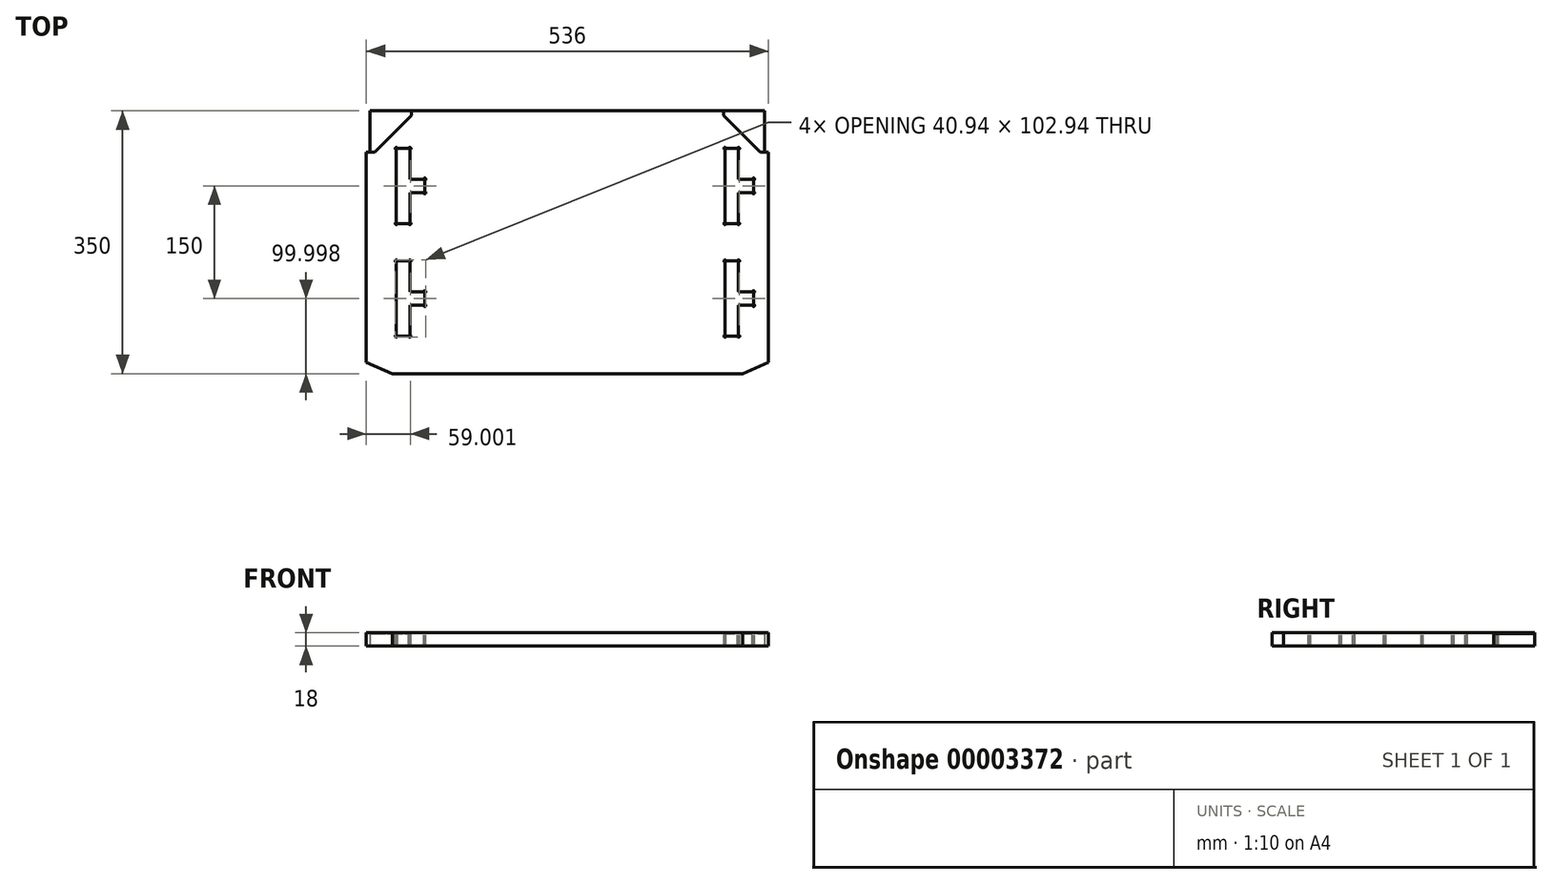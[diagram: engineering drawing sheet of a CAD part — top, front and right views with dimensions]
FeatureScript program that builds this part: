
annotation { "Feature Type Name" : "Feature", "Feature Type Description" : "" }
export const myFeature = defineFeature(function(context is Context, id is Id, definition is map)
    precondition{}
    {
        {
            var Q0;
            Q0=qCreatedBy(makeId("Top.planeOp"),FACE);
            var sketch = newSketch(context, id + "F0", { "sketchPlane" : qUnion([Q0])});
            skLineSegment(sketch, "E0.bottom", {"start": v(-215.74, -76.17) * mm, "end": v(320.26, -76.17) * mm});
            skLineSegment(sketch, "E0.top", {"start": v(-210.74, 273.83) * mm, "end": v(315.26, 273.83) * mm});
            skLineSegment(sketch, "E0.left", {"start": v(-215.74, -76.17) * mm, "end": v(-215.74, 218.83) * mm});
            skLineSegment(sketch, "E0.right", {"start": v(320.26, -76.17) * mm, "end": v(320.26, 218.83) * mm});
            skLineSegment(sketch, "E1.bottom", {"start": v(-175.74, -26.17) * mm, "end": v(-157.74, -26.17) * mm});
            skLineSegment(sketch, "E1.top", {"start": v(-175.74, 73.83) * mm, "end": v(-157.74, 73.83) * mm});
            skLineSegment(sketch, "E1.left", {"start": v(-175.74, -26.17) * mm, "end": v(-175.74, 73.83) * mm});
            skLineSegment(sketch, "E1.right", {"start": v(-157.74, -26.17) * mm, "end": v(-157.74, 14.83) * mm});
            skLineSegment(sketch, "E2.bottom", {"start": v(-175.74, 123.83) * mm, "end": v(-157.74, 123.83) * mm});
            skLineSegment(sketch, "E2.top", {"start": v(-175.74, 223.83) * mm, "end": v(-157.74, 223.83) * mm});
            skLineSegment(sketch, "E2.left", {"start": v(-175.74, 123.83) * mm, "end": v(-175.74, 223.83) * mm});
            skLineSegment(sketch, "E2.right", {"start": v(-157.74, 123.83) * mm, "end": v(-157.74, 164.83) * mm});
            skLineSegment(sketch, "E3.bottom", {"start": v(280.26, -26.17) * mm, "end": v(262.26, -26.17) * mm});
            skLineSegment(sketch, "E3.top", {"start": v(280.26, 73.83) * mm, "end": v(262.26, 73.83) * mm});
            skLineSegment(sketch, "E3.left", {"start": v(280.26, -26.17) * mm, "end": v(280.26, 14.83) * mm});
            skLineSegment(sketch, "E4.bottom", {"start": v(262.26, 223.83) * mm, "end": v(280.26, 223.83) * mm});
            skLineSegment(sketch, "E4.top", {"start": v(262.26, 123.83) * mm, "end": v(280.26, 123.83) * mm});
            skLineSegment(sketch, "E4.right", {"start": v(280.26, 223.83) * mm, "end": v(280.26, 182.83) * mm});
            skLineSegment(sketch, "E5", {"start": v(-157.74, 14.83) * mm, "end": v(-137.74, 14.83) * mm});
            skLineSegment(sketch, "E6", {"start": v(-137.74, 14.83) * mm, "end": v(-137.74, 32.83) * mm});
            skLineSegment(sketch, "E7", {"start": v(-137.74, 32.83) * mm, "end": v(-157.74, 32.83) * mm});
            skLineSegment(sketch, "E8.trimOffspring", {"start": v(-157.74, 32.83) * mm, "end": v(-157.74, 73.83) * mm});
            skLineSegment(sketch, "E9", {"start": v(-157.74, 164.83) * mm, "end": v(-137.74, 164.83) * mm});
            skLineSegment(sketch, "E10", {"start": v(-137.74, 164.83) * mm, "end": v(-137.74, 182.83) * mm});
            skLineSegment(sketch, "E11", {"start": v(-137.74, 182.83) * mm, "end": v(-157.74, 182.83) * mm});
            skLineSegment(sketch, "E12.trimOffspring", {"start": v(-157.74, 182.83) * mm, "end": v(-157.74, 223.83) * mm});
            skLineSegment(sketch, "E13", {"start": v(262.26, -26.17) * mm, "end": v(262.26, 73.83) * mm});
            skLineSegment(sketch, "E14", {"start": v(262.26, 123.83) * mm, "end": v(262.26, 223.83) * mm});
            skLineSegment(sketch, "E15.bottom", {"start": v(280.26, 14.83) * mm, "end": v(300.26, 14.83) * mm});
            skLineSegment(sketch, "E15.top", {"start": v(280.26, 32.83) * mm, "end": v(300.26, 32.83) * mm});
            skLineSegment(sketch, "E15.right", {"start": v(300.26, 14.83) * mm, "end": v(300.26, 32.83) * mm});
            skLineSegment(sketch, "E16.bottom", {"start": v(280.26, 164.83) * mm, "end": v(300.26, 164.83) * mm});
            skLineSegment(sketch, "E16.top", {"start": v(280.26, 182.83) * mm, "end": v(300.26, 182.83) * mm});
            skLineSegment(sketch, "E16.right", {"start": v(300.26, 164.83) * mm, "end": v(300.26, 182.83) * mm});
            skLineSegment(sketch, "E17.trimOffspring", {"start": v(280.26, 32.83) * mm, "end": v(280.26, 73.83) * mm});
            skLineSegment(sketch, "E18.trimOffspring", {"start": v(280.26, 164.83) * mm, "end": v(280.26, 123.83) * mm});
            skLineSegment(sketch, "E19.top", {"start": v(320.26, 218.83) * mm, "end": v(315.26, 218.83) * mm});
            skLineSegment(sketch, "E19.right", {"start": v(315.26, 273.83) * mm, "end": v(315.26, 218.83) * mm});
            skPoint(sketch, "E19.bottom.start.orphan", {"position": v(320.26, 273.83) * mm});
            skLineSegment(sketch, "E20.top", {"start": v(-215.74, 218.83) * mm, "end": v(-210.74, 218.83) * mm});
            skLineSegment(sketch, "E20.right", {"start": v(-210.74, 273.83) * mm, "end": v(-210.74, 218.83) * mm});
            skSolve(sketch);
        }
        {
            var Q0;
            Q0=makeQuery(id+"F0.imprint","IMPRINT",FACE,{"disambiguationData":[TD([[makeQuery(id+"F0.imprint","IMPRINT",EDGE,{"derivedFrom":sQuery(id+"F0.wireOp",EDGE,"E0.bottom")}),1.0]])]});
            extrude(context, id + "F1", {"entities" : qUnion([Q0]), "depth" : 18 * mm});
        }
        {
            var Q0;
            Q0=makeQuery(id+"F1.opExtrude","SWEPT_EDGE",EDGE,{"disambiguationData":[OSD([sQuery(id+"F0.wireOp",EDGE,"E0.bottom"),sQuery(id+"F0.wireOp",EDGE,"E0.left")])]});
            var Q1;
            Q1=makeQuery(id+"F1.opExtrude","SWEPT_EDGE",EDGE,{"disambiguationData":[OSD([sQuery(id+"F0.wireOp",EDGE,"E0.bottom"),sQuery(id+"F0.wireOp",EDGE,"E0.right")])]});
            chamfer(context, id + "F2", {"entities" : qUnion([Q0, Q1]), "chamferType" : ChamferType.TWO_OFFSETS, "width1" : 15 * mm, "oppositeDirection" : true, "width2" : 34.5 * mm, "tangentPropagation" : true});
        }
        {
            var Q0;
            Q0=makeQuery(id+"F1.opExtrude","CAP_FACE",FACE,{"disambiguationData":[OSD([sQuery(id+"F0.wireOp",EDGE,"E0.bottom"),sQuery(id+"F0.wireOp",EDGE,"E0.top"),sQuery(id+"F0.wireOp",EDGE,"E0.left"),sQuery(id+"F0.wireOp",EDGE,"E0.right"),sQuery(id+"F0.wireOp",EDGE,"E1.bottom"),sQuery(id+"F0.wireOp",EDGE,"E1.top"),sQuery(id+"F0.wireOp",EDGE,"E1.left"),sQuery(id+"F0.wireOp",EDGE,"E1.right"),sQuery(id+"F0.wireOp",EDGE,"E2.bottom"),sQuery(id+"F0.wireOp",EDGE,"E2.top"),sQuery(id+"F0.wireOp",EDGE,"E2.left"),sQuery(id+"F0.wireOp",EDGE,"E2.right"),sQuery(id+"F0.wireOp",EDGE,"E3.bottom"),sQuery(id+"F0.wireOp",EDGE,"E3.top"),sQuery(id+"F0.wireOp",EDGE,"E3.left"),sQuery(id+"F0.wireOp",EDGE,"E4.bottom"),sQuery(id+"F0.wireOp",EDGE,"E4.top"),sQuery(id+"F0.wireOp",EDGE,"E4.right"),sQuery(id+"F0.wireOp",EDGE,"E5"),sQuery(id+"F0.wireOp",EDGE,"E6"),sQuery(id+"F0.wireOp",EDGE,"E7"),sQuery(id+"F0.wireOp",EDGE,"E8.trimOffspring"),sQuery(id+"F0.wireOp",EDGE,"E9"),sQuery(id+"F0.wireOp",EDGE,"E10"),sQuery(id+"F0.wireOp",EDGE,"E11"),sQuery(id+"F0.wireOp",EDGE,"E12.trimOffspring"),sQuery(id+"F0.wireOp",EDGE,"E13"),sQuery(id+"F0.wireOp",EDGE,"E14"),sQuery(id+"F0.wireOp",EDGE,"E15.bottom"),sQuery(id+"F0.wireOp",EDGE,"E15.top"),sQuery(id+"F0.wireOp",EDGE,"E15.right"),sQuery(id+"F0.wireOp",EDGE,"E16.bottom"),sQuery(id+"F0.wireOp",EDGE,"E16.top"),sQuery(id+"F0.wireOp",EDGE,"E16.right"),sQuery(id+"F0.wireOp",EDGE,"E17.trimOffspring"),sQuery(id+"F0.wireOp",EDGE,"E18.trimOffspring"),sQuery(id+"F0.wireOp",EDGE,"E19.top"),sQuery(id+"F0.wireOp",EDGE,"E19.right"),sQuery(id+"F0.wireOp",EDGE,"E20.top"),sQuery(id+"F0.wireOp",EDGE,"E20.right")])],"isStart":false});
            var sketch = newSketch(context, id + "F3", { "sketchPlane" : qUnion([Q0])});
            skLineSegment(sketch, "E21", {"start": v(-210.74, 218.83) * mm, "end": v(-204.74, 218.83) * mm});
            skLineSegment(sketch, "E22", {"start": v(-204.74, 218.83) * mm, "end": v(-155.74, 267.83) * mm});
            skLineSegment(sketch, "E23", {"start": v(-155.74, 267.83) * mm, "end": v(-155.74, 273.83) * mm});
            skLineSegment(sketch, "E24", {"start": v(315.26, 218.83) * mm, "end": v(309.26, 218.83) * mm});
            skLineSegment(sketch, "E25", {"start": v(309.26, 218.83) * mm, "end": v(260.26, 267.83) * mm});
            skLineSegment(sketch, "E26", {"start": v(260.26, 267.83) * mm, "end": v(260.26, 273.83) * mm});
            skSolve(sketch);
        }
        {
            var Q0;
            Q0 = qSketchRegion(id + "F3", true);
            var Q1;
            Q1=makeQuery(id+"F3.imprint","IMPRINT",FACE,{"disambiguationData":[TD([[makeQuery(id+"F3.imprint","IMPRINT",EDGE,{"derivedFrom":sQuery(id+"F3.wireOp",EDGE,"E21")}),1.0]])]});
            var Q2;
            Q2=makeQuery(id+"F3.imprint","IMPRINT",FACE,{"disambiguationData":[TD([[makeQuery(id+"F3.imprint","IMPRINT",EDGE,{"derivedFrom":sQuery(id+"F3.wireOp",EDGE,"E24")}),-1.0]])]});
            extrude(context, id + "F4", {"entities" : qUnion([Q0, Q1, Q2]), "operationType" : NewBodyOperationType.REMOVE, "oppositeDirection" : true, "depth" : 1.5 * mm});
        }
        {
            var Q0;
            Q0=makeQuery(id+"F1.opExtrude","CAP_FACE",FACE,{"disambiguationData":[OSD([sQuery(id+"F0.wireOp",EDGE,"E0.bottom"),sQuery(id+"F0.wireOp",EDGE,"E0.top"),sQuery(id+"F0.wireOp",EDGE,"E0.left"),sQuery(id+"F0.wireOp",EDGE,"E0.right"),sQuery(id+"F0.wireOp",EDGE,"E1.bottom"),sQuery(id+"F0.wireOp",EDGE,"E1.top"),sQuery(id+"F0.wireOp",EDGE,"E1.left"),sQuery(id+"F0.wireOp",EDGE,"E1.right"),sQuery(id+"F0.wireOp",EDGE,"E2.bottom"),sQuery(id+"F0.wireOp",EDGE,"E2.top"),sQuery(id+"F0.wireOp",EDGE,"E2.left"),sQuery(id+"F0.wireOp",EDGE,"E2.right"),sQuery(id+"F0.wireOp",EDGE,"E3.bottom"),sQuery(id+"F0.wireOp",EDGE,"E3.top"),sQuery(id+"F0.wireOp",EDGE,"E3.left"),sQuery(id+"F0.wireOp",EDGE,"E4.bottom"),sQuery(id+"F0.wireOp",EDGE,"E4.top"),sQuery(id+"F0.wireOp",EDGE,"E4.right"),sQuery(id+"F0.wireOp",EDGE,"E5"),sQuery(id+"F0.wireOp",EDGE,"E6"),sQuery(id+"F0.wireOp",EDGE,"E7"),sQuery(id+"F0.wireOp",EDGE,"E8.trimOffspring"),sQuery(id+"F0.wireOp",EDGE,"E9"),sQuery(id+"F0.wireOp",EDGE,"E10"),sQuery(id+"F0.wireOp",EDGE,"E11"),sQuery(id+"F0.wireOp",EDGE,"E12.trimOffspring"),sQuery(id+"F0.wireOp",EDGE,"E13"),sQuery(id+"F0.wireOp",EDGE,"E14"),sQuery(id+"F0.wireOp",EDGE,"E15.bottom"),sQuery(id+"F0.wireOp",EDGE,"E15.top"),sQuery(id+"F0.wireOp",EDGE,"E15.right"),sQuery(id+"F0.wireOp",EDGE,"E16.bottom"),sQuery(id+"F0.wireOp",EDGE,"E16.top"),sQuery(id+"F0.wireOp",EDGE,"E16.right"),sQuery(id+"F0.wireOp",EDGE,"E17.trimOffspring"),sQuery(id+"F0.wireOp",EDGE,"E18.trimOffspring"),sQuery(id+"F0.wireOp",EDGE,"E19.top"),sQuery(id+"F0.wireOp",EDGE,"E19.right"),sQuery(id+"F0.wireOp",EDGE,"E20.top"),sQuery(id+"F0.wireOp",EDGE,"E20.right")])],"isStart":false});
            var sketch = newSketch(context, id + "F5", { "sketchPlane" : qUnion([Q0])});
            skCircle(sketch, "E27", {"center": v(-157.74, -26.17) * mm, "radius": 1.5 * mm});
            skCircle(sketch, "E28", {"center": v(-175.74, -26.17) * mm, "radius": 1.5 * mm});
            skCircle(sketch, "E29", {"center": v(-175.74, 73.83) * mm, "radius": 1.5 * mm});
            skCircle(sketch, "E30", {"center": v(-137.74, 32.83) * mm, "radius": 1.5 * mm});
            skCircle(sketch, "E31", {"center": v(-137.74, 14.83) * mm, "radius": 1.5 * mm});
            skCircle(sketch, "E32", {"center": v(-137.74, 164.83) * mm, "radius": 1.5 * mm});
            skCircle(sketch, "E33", {"center": v(-137.74, 182.83) * mm, "radius": 1.5 * mm});
            skCircle(sketch, "E34", {"center": v(-157.74, 123.83) * mm, "radius": 1.5 * mm});
            skCircle(sketch, "E35", {"center": v(-175.74, 123.83) * mm, "radius": 1.5 * mm});
            skCircle(sketch, "E36", {"center": v(280.26, -26.17) * mm, "radius": 1.5 * mm});
            skCircle(sketch, "E37", {"center": v(262.26, -26.17) * mm, "radius": 1.5 * mm});
            skCircle(sketch, "E38", {"center": v(300.26, 14.83) * mm, "radius": 1.5 * mm});
            skCircle(sketch, "E39", {"center": v(300.26, 32.83) * mm, "radius": 1.5 * mm});
            skCircle(sketch, "E40", {"center": v(280.26, 73.83) * mm, "radius": 1.5 * mm});
            skCircle(sketch, "E41", {"center": v(262.26, 73.83) * mm, "radius": 1.5 * mm});
            skCircle(sketch, "E42", {"center": v(300.26, 164.83) * mm, "radius": 1.5 * mm});
            skCircle(sketch, "E43", {"center": v(300.26, 182.83) * mm, "radius": 1.5 * mm});
            skCircle(sketch, "E44", {"center": v(280.26, 223.83) * mm, "radius": 1.5 * mm});
            skCircle(sketch, "E45", {"center": v(262.26, 223.83) * mm, "radius": 1.5 * mm});
            skCircle(sketch, "E46", {"center": v(262.26, 123.83) * mm, "radius": 1.5 * mm});
            skCircle(sketch, "E47", {"center": v(280.26, 123.83) * mm, "radius": 1.5 * mm});
            skCircle(sketch, "E48", {"center": v(-157.74, 223.83) * mm, "radius": 1.5 * mm});
            skCircle(sketch, "E49", {"center": v(-175.74, 223.83) * mm, "radius": 1.5 * mm});
            skCircle(sketch, "E50", {"center": v(-157.74, 73.83) * mm, "radius": 1.5 * mm});
            skSolve(sketch);
        }
        {
            var Q0;
            {var subQ1=sQuery(id+"F5.wireOp",EDGE,"E27");var subQ3=makeQuery(id+"F1.opExtrude","CAP_EDGE",EDGE,{"disambiguationData":[OSD([sQuery(id+"F0.wireOp",EDGE,"E1.bottom")])],"isStart":false});var subQ6=makeQuery(id+"F5.imprint","INTERSECT",VERTEX,{"derivedFrom":[subQ3,subQ1]});var subQ9=sQuery(id+"F5.wireOp",EDGE,"E28");var subQ13=makeQuery(id+"F5.imprint","INTERSECT",VERTEX,{"derivedFrom":[subQ3,subQ9]});var subQ15=sQuery(id+"F5.wireOp",EDGE,"E29");var subQ17=makeQuery(id+"F1.opExtrude","CAP_EDGE",EDGE,{"disambiguationData":[OSD([sQuery(id+"F0.wireOp",EDGE,"E1.top")])],"isStart":false});var subQ20=makeQuery(id+"F5.imprint","INTERSECT",VERTEX,{"derivedFrom":[subQ17,subQ15]});var subQ23=sQuery(id+"F5.wireOp",EDGE,"E30");var subQ25=makeQuery(id+"F1.opExtrude","CAP_EDGE",EDGE,{"disambiguationData":[OSD([sQuery(id+"F0.wireOp",EDGE,"E6")])],"isStart":false});var subQ28=makeQuery(id+"F5.imprint","INTERSECT",VERTEX,{"derivedFrom":[subQ25,subQ23]});var subQ30=sQuery(id+"F5.wireOp",EDGE,"E31");var subQ32=makeQuery(id+"F1.opExtrude","CAP_EDGE",EDGE,{"disambiguationData":[OSD([sQuery(id+"F0.wireOp",EDGE,"E5")])],"isStart":false});var subQ35=makeQuery(id+"F5.imprint","INTERSECT",VERTEX,{"derivedFrom":[subQ32,subQ30]});var subQ37=makeQuery(id+"F1.opExtrude","CAP_EDGE",EDGE,{"disambiguationData":[OSD([sQuery(id+"F0.wireOp",EDGE,"E10")])],"isStart":false});var subQ38=sQuery(id+"F5.wireOp",EDGE,"E32");var subQ40=makeQuery(id+"F1.opExtrude","CAP_EDGE",EDGE,{"disambiguationData":[OSD([sQuery(id+"F0.wireOp",EDGE,"E9")])],"isStart":false});var subQ43=makeQuery(id+"F5.imprint","INTERSECT",VERTEX,{"derivedFrom":[subQ40,subQ38]});var subQ45=sQuery(id+"F5.wireOp",EDGE,"E33");var subQ46=makeQuery(id+"F5.imprint","INTERSECT",VERTEX,{"derivedFrom":[subQ37,subQ45]});var subQ53=sQuery(id+"F5.wireOp",EDGE,"E34");var subQ55=makeQuery(id+"F1.opExtrude","CAP_EDGE",EDGE,{"disambiguationData":[OSD([sQuery(id+"F0.wireOp",EDGE,"E2.bottom")])],"isStart":false});var subQ58=makeQuery(id+"F5.imprint","INTERSECT",VERTEX,{"derivedFrom":[subQ55,subQ53]});var subQ61=sQuery(id+"F5.wireOp",EDGE,"E35");var subQ65=makeQuery(id+"F5.imprint","INTERSECT",VERTEX,{"derivedFrom":[subQ55,subQ61]});var subQ68=sQuery(id+"F5.wireOp",EDGE,"E36");var subQ70=makeQuery(id+"F1.opExtrude","CAP_EDGE",EDGE,{"disambiguationData":[OSD([sQuery(id+"F0.wireOp",EDGE,"E3.bottom")])],"isStart":false});var subQ73=makeQuery(id+"F5.imprint","INTERSECT",VERTEX,{"derivedFrom":[subQ70,subQ68]});var subQ76=sQuery(id+"F5.wireOp",EDGE,"E37");var subQ80=makeQuery(id+"F5.imprint","INTERSECT",VERTEX,{"derivedFrom":[subQ70,subQ76]});var subQ83=sQuery(id+"F5.wireOp",EDGE,"E38");var subQ85=makeQuery(id+"F1.opExtrude","CAP_EDGE",EDGE,{"disambiguationData":[OSD([sQuery(id+"F0.wireOp",EDGE,"E15.bottom")])],"isStart":false});var subQ88=makeQuery(id+"F5.imprint","INTERSECT",VERTEX,{"derivedFrom":[subQ85,subQ83]});var subQ90=sQuery(id+"F5.wireOp",EDGE,"E39");var subQ92=makeQuery(id+"F1.opExtrude","CAP_EDGE",EDGE,{"disambiguationData":[OSD([sQuery(id+"F0.wireOp",EDGE,"E15.top")])],"isStart":false});var subQ95=makeQuery(id+"F5.imprint","INTERSECT",VERTEX,{"derivedFrom":[subQ92,subQ90]});var subQ98=sQuery(id+"F5.wireOp",EDGE,"E40");var subQ100=makeQuery(id+"F1.opExtrude","CAP_EDGE",EDGE,{"disambiguationData":[OSD([sQuery(id+"F0.wireOp",EDGE,"E3.top")])],"isStart":false});var subQ103=makeQuery(id+"F5.imprint","INTERSECT",VERTEX,{"derivedFrom":[subQ100,subQ98]});var subQ105=sQuery(id+"F5.wireOp",EDGE,"E41");var subQ109=makeQuery(id+"F5.imprint","INTERSECT",VERTEX,{"derivedFrom":[subQ100,subQ105]});var subQ112=sQuery(id+"F5.wireOp",EDGE,"E42");var subQ114=makeQuery(id+"F1.opExtrude","CAP_EDGE",EDGE,{"disambiguationData":[OSD([sQuery(id+"F0.wireOp",EDGE,"E16.bottom")])],"isStart":false});var subQ117=makeQuery(id+"F5.imprint","INTERSECT",VERTEX,{"derivedFrom":[subQ114,subQ112]});var subQ119=sQuery(id+"F5.wireOp",EDGE,"E43");var subQ121=makeQuery(id+"F1.opExtrude","CAP_EDGE",EDGE,{"disambiguationData":[OSD([sQuery(id+"F0.wireOp",EDGE,"E16.top")])],"isStart":false});var subQ124=makeQuery(id+"F5.imprint","INTERSECT",VERTEX,{"derivedFrom":[subQ121,subQ119]});var subQ127=sQuery(id+"F5.wireOp",EDGE,"E44");var subQ129=makeQuery(id+"F1.opExtrude","CAP_EDGE",EDGE,{"disambiguationData":[OSD([sQuery(id+"F0.wireOp",EDGE,"E4.bottom")])],"isStart":false});var subQ132=makeQuery(id+"F5.imprint","INTERSECT",VERTEX,{"derivedFrom":[subQ129,subQ127]});var subQ135=sQuery(id+"F5.wireOp",EDGE,"E45");var subQ139=makeQuery(id+"F5.imprint","INTERSECT",VERTEX,{"derivedFrom":[subQ129,subQ135]});var subQ141=sQuery(id+"F5.wireOp",EDGE,"E46");var subQ143=makeQuery(id+"F1.opExtrude","CAP_EDGE",EDGE,{"disambiguationData":[OSD([sQuery(id+"F0.wireOp",EDGE,"E4.top")])],"isStart":false});var subQ146=makeQuery(id+"F5.imprint","INTERSECT",VERTEX,{"derivedFrom":[subQ143,subQ141]});var subQ149=sQuery(id+"F5.wireOp",EDGE,"E47");var subQ153=makeQuery(id+"F5.imprint","INTERSECT",VERTEX,{"derivedFrom":[subQ143,subQ149]});var subQ156=sQuery(id+"F5.wireOp",EDGE,"E48");var subQ158=makeQuery(id+"F1.opExtrude","CAP_EDGE",EDGE,{"disambiguationData":[OSD([sQuery(id+"F0.wireOp",EDGE,"E2.top")])],"isStart":false});var subQ161=makeQuery(id+"F5.imprint","INTERSECT",VERTEX,{"derivedFrom":[subQ158,subQ156]});var subQ163=sQuery(id+"F5.wireOp",EDGE,"E49");var subQ167=makeQuery(id+"F5.imprint","INTERSECT",VERTEX,{"derivedFrom":[subQ158,subQ163]});var subQ170=sQuery(id+"F5.wireOp",EDGE,"E50");var subQ174=makeQuery(id+"F5.imprint","INTERSECT",VERTEX,{"derivedFrom":[subQ17,subQ170]});Q0=qUnion([makeQuery(id+"F5.imprint","IMPRINT",FACE,{"disambiguationData":[TD([[makeQuery(id+"F5.imprint","IMPRINT",EDGE,{"disambiguationData":[TD([[subQ6,1.0]])],"derivedFrom":subQ1}),1.0]])]}),makeQuery(id+"F5.imprint","IMPRINT",FACE,{"disambiguationData":[TD([[makeQuery(id+"F5.imprint","IMPRINT",EDGE,{"disambiguationData":[TD([[subQ6,-1.0]])],"derivedFrom":subQ1}),1.0]])]}),makeQuery(id+"F5.imprint","IMPRINT",FACE,{"disambiguationData":[TD([[makeQuery(id+"F5.imprint","IMPRINT",EDGE,{"disambiguationData":[TD([[subQ13,-1.0]])],"derivedFrom":subQ9}),1.0]])]}),makeQuery(id+"F5.imprint","IMPRINT",FACE,{"disambiguationData":[TD([[makeQuery(id+"F5.imprint","IMPRINT",EDGE,{"disambiguationData":[TD([[subQ13,1.0]])],"derivedFrom":subQ9}),1.0]])]}),makeQuery(id+"F5.imprint","IMPRINT",FACE,{"disambiguationData":[TD([[makeQuery(id+"F5.imprint","IMPRINT",EDGE,{"disambiguationData":[TD([[subQ20,-1.0]])],"derivedFrom":subQ15}),1.0]])]}),makeQuery(id+"F5.imprint","IMPRINT",FACE,{"disambiguationData":[TD([[makeQuery(id+"F5.imprint","IMPRINT",EDGE,{"disambiguationData":[TD([[subQ20,1.0]])],"derivedFrom":subQ15}),1.0]])]}),makeQuery(id+"F5.imprint","IMPRINT",FACE,{"disambiguationData":[TD([[makeQuery(id+"F5.imprint","IMPRINT",EDGE,{"disambiguationData":[TD([[subQ28,1.0]])],"derivedFrom":subQ23}),1.0]])]}),makeQuery(id+"F5.imprint","IMPRINT",FACE,{"disambiguationData":[TD([[makeQuery(id+"F5.imprint","IMPRINT",EDGE,{"disambiguationData":[TD([[subQ28,-1.0]])],"derivedFrom":subQ23}),1.0]])]}),makeQuery(id+"F5.imprint","IMPRINT",FACE,{"disambiguationData":[TD([[makeQuery(id+"F5.imprint","IMPRINT",EDGE,{"disambiguationData":[TD([[subQ35,1.0]])],"derivedFrom":subQ30}),1.0]])]}),makeQuery(id+"F5.imprint","IMPRINT",FACE,{"disambiguationData":[TD([[makeQuery(id+"F5.imprint","IMPRINT",EDGE,{"disambiguationData":[TD([[subQ35,-1.0]])],"derivedFrom":subQ30}),1.0]])]}),makeQuery(id+"F5.imprint","IMPRINT",FACE,{"disambiguationData":[TD([[makeQuery(id+"F5.imprint","IMPRINT",EDGE,{"disambiguationData":[TD([[subQ43,1.0]])],"derivedFrom":subQ38}),1.0]])]}),makeQuery(id+"F5.imprint","IMPRINT",FACE,{"disambiguationData":[TD([[makeQuery(id+"F5.imprint","IMPRINT",EDGE,{"disambiguationData":[TD([[subQ43,-1.0]])],"derivedFrom":subQ38}),1.0]])]}),makeQuery(id+"F5.imprint","IMPRINT",FACE,{"disambiguationData":[TD([[makeQuery(id+"F5.imprint","IMPRINT",EDGE,{"disambiguationData":[TD([[subQ46,1.0]])],"derivedFrom":subQ45}),1.0]])]}),makeQuery(id+"F5.imprint","IMPRINT",FACE,{"disambiguationData":[TD([[makeQuery(id+"F5.imprint","IMPRINT",EDGE,{"disambiguationData":[TD([[subQ46,-1.0]])],"derivedFrom":subQ45}),1.0]])]}),makeQuery(id+"F5.imprint","IMPRINT",FACE,{"disambiguationData":[TD([[makeQuery(id+"F5.imprint","IMPRINT",EDGE,{"disambiguationData":[TD([[subQ58,1.0]])],"derivedFrom":subQ53}),1.0]])]}),makeQuery(id+"F5.imprint","IMPRINT",FACE,{"disambiguationData":[TD([[makeQuery(id+"F5.imprint","IMPRINT",EDGE,{"disambiguationData":[TD([[subQ58,-1.0]])],"derivedFrom":subQ53}),1.0]])]}),makeQuery(id+"F5.imprint","IMPRINT",FACE,{"disambiguationData":[TD([[makeQuery(id+"F5.imprint","IMPRINT",EDGE,{"disambiguationData":[TD([[subQ65,-1.0]])],"derivedFrom":subQ61}),1.0]])]}),makeQuery(id+"F5.imprint","IMPRINT",FACE,{"disambiguationData":[TD([[makeQuery(id+"F5.imprint","IMPRINT",EDGE,{"disambiguationData":[TD([[subQ65,1.0]])],"derivedFrom":subQ61}),1.0]])]}),makeQuery(id+"F5.imprint","IMPRINT",FACE,{"disambiguationData":[TD([[makeQuery(id+"F5.imprint","IMPRINT",EDGE,{"disambiguationData":[TD([[subQ73,1.0]])],"derivedFrom":subQ68}),1.0]])]}),makeQuery(id+"F5.imprint","IMPRINT",FACE,{"disambiguationData":[TD([[makeQuery(id+"F5.imprint","IMPRINT",EDGE,{"disambiguationData":[TD([[subQ73,-1.0]])],"derivedFrom":subQ68}),1.0]])]}),makeQuery(id+"F5.imprint","IMPRINT",FACE,{"disambiguationData":[TD([[makeQuery(id+"F5.imprint","IMPRINT",EDGE,{"disambiguationData":[TD([[subQ80,-1.0]])],"derivedFrom":subQ76}),1.0]])]}),makeQuery(id+"F5.imprint","IMPRINT",FACE,{"disambiguationData":[TD([[makeQuery(id+"F5.imprint","IMPRINT",EDGE,{"disambiguationData":[TD([[subQ80,1.0]])],"derivedFrom":subQ76}),1.0]])]}),makeQuery(id+"F5.imprint","IMPRINT",FACE,{"disambiguationData":[TD([[makeQuery(id+"F5.imprint","IMPRINT",EDGE,{"disambiguationData":[TD([[subQ88,1.0]])],"derivedFrom":subQ83}),1.0]])]}),makeQuery(id+"F5.imprint","IMPRINT",FACE,{"disambiguationData":[TD([[makeQuery(id+"F5.imprint","IMPRINT",EDGE,{"disambiguationData":[TD([[subQ88,-1.0]])],"derivedFrom":subQ83}),1.0]])]}),makeQuery(id+"F5.imprint","IMPRINT",FACE,{"disambiguationData":[TD([[makeQuery(id+"F5.imprint","IMPRINT",EDGE,{"disambiguationData":[TD([[subQ95,-1.0]])],"derivedFrom":subQ90}),1.0]])]}),makeQuery(id+"F5.imprint","IMPRINT",FACE,{"disambiguationData":[TD([[makeQuery(id+"F5.imprint","IMPRINT",EDGE,{"disambiguationData":[TD([[subQ95,1.0]])],"derivedFrom":subQ90}),1.0]])]}),makeQuery(id+"F5.imprint","IMPRINT",FACE,{"disambiguationData":[TD([[makeQuery(id+"F5.imprint","IMPRINT",EDGE,{"disambiguationData":[TD([[subQ103,-1.0]])],"derivedFrom":subQ98}),1.0]])]}),makeQuery(id+"F5.imprint","IMPRINT",FACE,{"disambiguationData":[TD([[makeQuery(id+"F5.imprint","IMPRINT",EDGE,{"disambiguationData":[TD([[subQ103,1.0]])],"derivedFrom":subQ98}),1.0]])]}),makeQuery(id+"F5.imprint","IMPRINT",FACE,{"disambiguationData":[TD([[makeQuery(id+"F5.imprint","IMPRINT",EDGE,{"disambiguationData":[TD([[subQ109,-1.0]])],"derivedFrom":subQ105}),1.0]])]}),makeQuery(id+"F5.imprint","IMPRINT",FACE,{"disambiguationData":[TD([[makeQuery(id+"F5.imprint","IMPRINT",EDGE,{"disambiguationData":[TD([[subQ109,1.0]])],"derivedFrom":subQ105}),1.0]])]}),makeQuery(id+"F5.imprint","IMPRINT",FACE,{"disambiguationData":[TD([[makeQuery(id+"F5.imprint","IMPRINT",EDGE,{"disambiguationData":[TD([[subQ117,1.0]])],"derivedFrom":subQ112}),1.0]])]}),makeQuery(id+"F5.imprint","IMPRINT",FACE,{"disambiguationData":[TD([[makeQuery(id+"F5.imprint","IMPRINT",EDGE,{"disambiguationData":[TD([[subQ117,-1.0]])],"derivedFrom":subQ112}),1.0]])]}),makeQuery(id+"F5.imprint","IMPRINT",FACE,{"disambiguationData":[TD([[makeQuery(id+"F5.imprint","IMPRINT",EDGE,{"disambiguationData":[TD([[subQ124,-1.0]])],"derivedFrom":subQ119}),1.0]])]}),makeQuery(id+"F5.imprint","IMPRINT",FACE,{"disambiguationData":[TD([[makeQuery(id+"F5.imprint","IMPRINT",EDGE,{"disambiguationData":[TD([[subQ124,1.0]])],"derivedFrom":subQ119}),1.0]])]}),makeQuery(id+"F5.imprint","IMPRINT",FACE,{"disambiguationData":[TD([[makeQuery(id+"F5.imprint","IMPRINT",EDGE,{"disambiguationData":[TD([[subQ132,-1.0]])],"derivedFrom":subQ127}),1.0]])]}),makeQuery(id+"F5.imprint","IMPRINT",FACE,{"disambiguationData":[TD([[makeQuery(id+"F5.imprint","IMPRINT",EDGE,{"disambiguationData":[TD([[subQ132,1.0]])],"derivedFrom":subQ127}),1.0]])]}),makeQuery(id+"F5.imprint","IMPRINT",FACE,{"disambiguationData":[TD([[makeQuery(id+"F5.imprint","IMPRINT",EDGE,{"disambiguationData":[TD([[subQ139,-1.0]])],"derivedFrom":subQ135}),1.0]])]}),makeQuery(id+"F5.imprint","IMPRINT",FACE,{"disambiguationData":[TD([[makeQuery(id+"F5.imprint","IMPRINT",EDGE,{"disambiguationData":[TD([[subQ139,1.0]])],"derivedFrom":subQ135}),1.0]])]}),makeQuery(id+"F5.imprint","IMPRINT",FACE,{"disambiguationData":[TD([[makeQuery(id+"F5.imprint","IMPRINT",EDGE,{"disambiguationData":[TD([[subQ146,-1.0]])],"derivedFrom":subQ141}),1.0]])]}),makeQuery(id+"F5.imprint","IMPRINT",FACE,{"disambiguationData":[TD([[makeQuery(id+"F5.imprint","IMPRINT",EDGE,{"disambiguationData":[TD([[subQ146,1.0]])],"derivedFrom":subQ141}),1.0]])]}),makeQuery(id+"F5.imprint","IMPRINT",FACE,{"disambiguationData":[TD([[makeQuery(id+"F5.imprint","IMPRINT",EDGE,{"disambiguationData":[TD([[subQ153,1.0]])],"derivedFrom":subQ149}),1.0]])]}),makeQuery(id+"F5.imprint","IMPRINT",FACE,{"disambiguationData":[TD([[makeQuery(id+"F5.imprint","IMPRINT",EDGE,{"disambiguationData":[TD([[subQ153,-1.0]])],"derivedFrom":subQ149}),1.0]])]}),makeQuery(id+"F5.imprint","IMPRINT",FACE,{"disambiguationData":[TD([[makeQuery(id+"F5.imprint","IMPRINT",EDGE,{"disambiguationData":[TD([[subQ161,-1.0]])],"derivedFrom":subQ156}),1.0]])]}),makeQuery(id+"F5.imprint","IMPRINT",FACE,{"disambiguationData":[TD([[makeQuery(id+"F5.imprint","IMPRINT",EDGE,{"disambiguationData":[TD([[subQ161,1.0]])],"derivedFrom":subQ156}),1.0]])]}),makeQuery(id+"F5.imprint","IMPRINT",FACE,{"disambiguationData":[TD([[makeQuery(id+"F5.imprint","IMPRINT",EDGE,{"disambiguationData":[TD([[subQ167,-1.0]])],"derivedFrom":subQ163}),1.0]])]}),makeQuery(id+"F5.imprint","IMPRINT",FACE,{"disambiguationData":[TD([[makeQuery(id+"F5.imprint","IMPRINT",EDGE,{"disambiguationData":[TD([[subQ167,1.0]])],"derivedFrom":subQ163}),1.0]])]}),makeQuery(id+"F5.imprint","IMPRINT",FACE,{"disambiguationData":[TD([[makeQuery(id+"F5.imprint","IMPRINT",EDGE,{"disambiguationData":[TD([[subQ174,-1.0]])],"derivedFrom":subQ170}),1.0]])]}),makeQuery(id+"F5.imprint","IMPRINT",FACE,{"disambiguationData":[TD([[makeQuery(id+"F5.imprint","IMPRINT",EDGE,{"disambiguationData":[TD([[subQ174,1.0]])],"derivedFrom":subQ170}),1.0]])]})]);}
            extrude(context, id + "F6", {"entities" : qUnion([Q0]), "operationType" : NewBodyOperationType.REMOVE, "oppositeDirection" : true, "depth" : 25 * mm});
        }
    });
